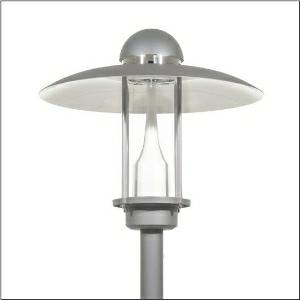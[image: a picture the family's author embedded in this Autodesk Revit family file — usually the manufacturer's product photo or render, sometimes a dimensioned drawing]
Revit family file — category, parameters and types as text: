
# Revit family: city-light_elegance_iq___pl1_2s_5xa5265rf14h_e1f1
name_source: partatom
category: Lighting Fixtures
units: mm (PartAtom-declared; Revit-internal decimal feet)

## family parameters
Cut with Voids When Loaded = No
Host = Face
Light Source = No
Part Type = Normal
Room Calculation Point = No
Round Connector Dimension = Use Diameter
Shared = No

## types (1)
- --- (1 x LED, 2840 lm, 18.5 W, 4000K)
    Apparent Load = 19 VA
    CIE Flux Codes = 24 63 94 98 100
    Color Rendering = 70
    Color Temperature = 4000K
    Default Elevation = 1800 mm
    Description = City-Light Elegance iQ, mast luminaire, Module 540 iQ-SR, primary light control with 3 zone facetted reflector, of plastic, silver coated, highly specular, structured, primary optical cover: cover, of PMMA, transparent, light distribution: PL1.2s, light emission: direct distribution, primary light characteristic: symmetric, installation type: post-top, LED, High Power LED, rated luminous flux: 2.840lm, luminous efficacy: 153lm/W, light colour: 740, colour temperature: 4000K, control gear: iQ Street-Remote, control: pre-setting: logarithmic dimming characteristic, Street-Remote, Auto-Match, Temp-Guard, Lumen-Switch, Night-Set, Smart-Wire, Light-Fading, Desk-Remote (wireless, voltage-free reading and setting of iQ features in the workshop via application-optimized NFC function/RFID function), optimised constant luminous flux control (CLO 2.0), with terminal, 6-pole, max. 2.5mm², mains connection: 230..240V, AC, 50/60Hz, start of lifetime: 19W, end of service life: 20W, reduction: 9W, luminaire housing, upper part, of aluminium, coated, Siteco® metallic grey (DB 702S), diameter: 750mm, height: 675mm, spigot size: d x l = 76 x 70mm (post-top) | with reducer (optional accessory) 60 x 70mm, mounting height: 3..5m, post-top mast mounting element, of diecast aluminium, coated, Siteco® metallic grey (DB 702S), Module 540 iQ-SR, traffic white (RAL 9016), equipment: standard, protection rating (complete): IP65, insulation class (complete): insulation class II (safety insulation), certification: CE, ENEC, VDE, packaging unit: 1 piece

Light Distribution: PL1.2s
    Height = 675 mm
    Lamp = 1 x LED
    Lamp Light Flux = 2840 lm
    Lamp Power = 18.5 W
    Lamp count = 1
    Length = 750 mm
    Luminous efficacy = 154 lm/W
    Manufacturer = Siteco
    ModVariant = No
    Model = 5XA5265RF14H
    Number of Poles = 1
    OnlyDefault = Yes
    Power Factor = 1
    Product Name = City-Light Elegance iQ | PL1.2s
    Product group = mast luminaire | pylon top
    ProductGroupID = 6100
    Protection Class = Protection class II
    Protection Degree = IP 65
    RLX_Detail_Level = 1
    RLX_Emergency_Light_Flux = 0 lm
    RLX_Emergency_Type = 0
    RLX_Emergency_Type_DB = No
    RlxData = <blob elided: 33585 chars, md5=cd6180ba>
    Socket = socket
    Standby Power = 0 W
    System Light Flux = 2840 lm
    System Power = 19 W
    Type Comments = factory setting: luminous flux: 100 % | dim-lin: 254 | 385 mA
    Type Image = l_1006912.jpg
    URL = http://relux.com
    VarID = @adj_145340
    Voltage = 0 V
    Weight = 0.00 kg
    Width = 0 mm  [stored 0 ft]

note: [stored X ft] marks values corroborated as IEEE doubles in the binary element streams (Revit-internal decimal feet)

## geometry (parser evidence)
native form markers: Blend x4, Sweep x10
no freeform markers — native parametric forms only
